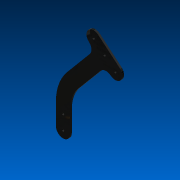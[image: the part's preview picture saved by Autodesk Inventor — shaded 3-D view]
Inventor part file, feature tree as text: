
AUTODESK INVENTOR PART (.ipt)
format: ipt  version: 2022 (Build 260153000, 153)  size: 129,024 bytes
history: native  units: in
note: dims shown in document units (in); Inventor stores cm internally (conversion verified against a paired STEP export)
features: extrude x1, hole x1, fillet x1
ambient origin geometry x8: Origin, YZ Plane, XZ Plane, XY Plane, X Axis, Y Axis, Z Axis, Center Point
bodies: Solid1 (feature_tree)
feature tree (3):
  extrude  "Extrusion1"  Depth=1.0in
  hole  "Hole1"  [1 undecoded]
  fillet  "Fillet1"  Radius=1.0in
note: 1 required parameter value undecoded (feature->parameter linkage not recoverable at this tier; creation-order binding heuristic only, values carry confidence <= 0.55)
